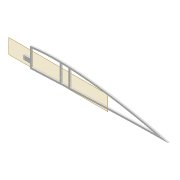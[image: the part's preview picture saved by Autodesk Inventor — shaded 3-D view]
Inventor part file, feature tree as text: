
AUTODESK INVENTOR PART (.ipt)
format: ipt  version: 2022 (Build 260153000, 153)  size: 421,888 bytes
history: native  units: mm
features: extrude x8, sketch x7, projected_geometry x6, fillet x2, shell x1, plane x1
ambient origin geometry x8: Origin, YZ Plane, XZ Plane, XY Plane, X Axis, Y Axis, Z Axis, Center Point
bodies: Solid1 (feature_tree)
feature tree (25):
  extrude  "Extrusion1"  Depth=5.0mm
  shell  "Shell1"  Thickness=2.0mm
  extrude  "Extrusion8"  Depth=5.9mm
  extrude  "Extrusion3"  Depth=10.0mm TaperAngle=0.0deg
  extrude  "Extrusion4"  Depth=2.0mm
  fillet  "Fillet1"  Radius=5.0mm
  sketch  "Sketch10"  dims[d22=4.0mm d23=0.0mm d31=2.0mm d32=5.0mm]
  extrude  "Extrusion5"  Depth=2.5mm
  plane  "Work Plane2"
  extrude  "Extrusion9"  Depth=1.6mm
  fillet  "Fillet2"  Radius=2.5mm
  extrude  "Extrusion10"  Depth=0.5mm
  extrude  "Extrusion11"  Depth=0.5mm TaperAngle=0.0deg
  sketch  "Sketch3"  dims[d0=4.0mm d1=0.0mm d2=5.0mm d7=2.0mm]
  sketch  "Sketch8"  dims[d8=2.0mm d9=5.9mm]
  sketch  "Sketch9"  dims[d13=10.0mm d14=0.0mm d16=10.0mm d17=0.0mm]
  projected_geometry  "Projected Loop4"
  projected_geometry  "Projected Loop10"
  sketch  "Sketch24"  dims[d34=1.6mm d35=2.5mm]
  projected_geometry  "Projected Loop11"
  projected_geometry  "Projected Loop12"
  projected_geometry  "Projected Loop13"
  sketch  "Sketch26"  dims[d37=5.0mm d38=1.6mm d40=2.5mm]
  projected_geometry  "Projected Loop14"
  sketch  "Sketch27"  dims[d62=80.0mm d63=6.0mm d64=4.0mm d65=0.0mm d66=3.0mm d67=12.0mm d68=5.0mm d69=19.0mm d70=12.0mm d71=3.05mm d72=10.0mm d73=0.0mm d74=2.0mm d75=100.0mm d76=20.0mm d77=0.5mm d78=10.0mm d79=0.0mm d80=10.0mm d81=0.0mm]
